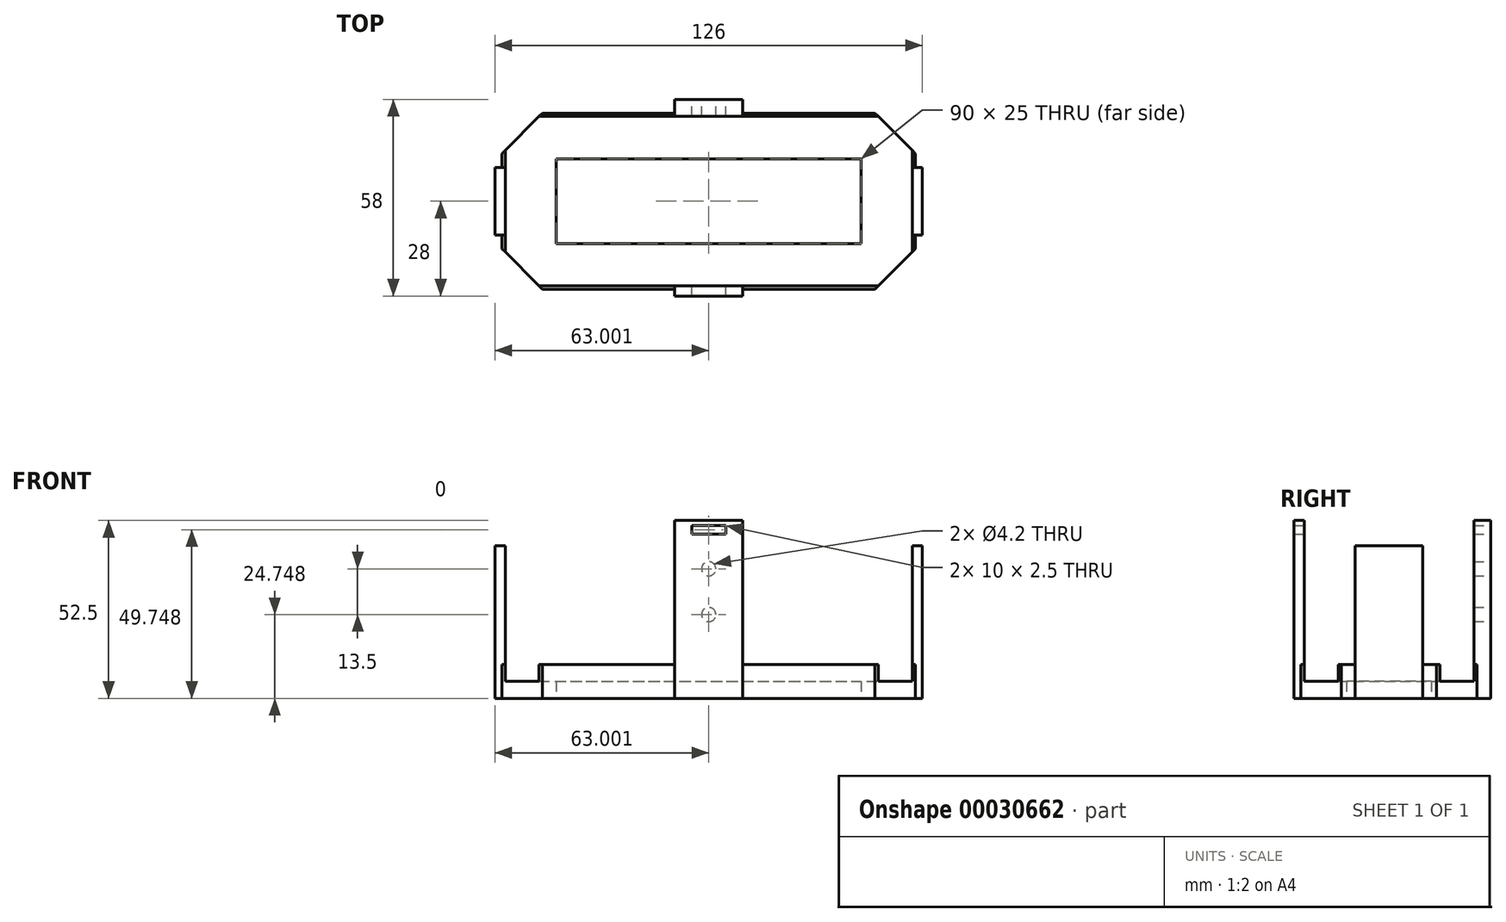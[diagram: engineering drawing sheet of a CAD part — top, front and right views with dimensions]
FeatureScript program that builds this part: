
annotation { "Feature Type Name" : "Feature", "Feature Type Description" : "" }
export const myFeature = defineFeature(function(context is Context, id is Id, definition is map)
    precondition{}
    {
        {
            var Q0;
            Q0=qCreatedBy(makeId("Front.planeOp"),FACE);
            var sketch = newSketch(context, id + "F0", { "sketchPlane" : qUnion([Q0])});
            skLineSegment(sketch, "E0.0.0", {"start": v(107.73, 27.2) * mm, "end": v(107.73, -17.8) * mm});
            skLineSegment(sketch, "E0.0.1", {"start": v(107.73, -17.8) * mm, "end": v(127.73, -17.8) * mm});
            skLineSegment(sketch, "E0.0.2", {"start": v(127.73, -17.8) * mm, "end": v(127.73, 27.2) * mm});
            skLineSegment(sketch, "E0.0.3", {"start": v(127.73, 27.2) * mm, "end": v(107.73, 27.2) * mm});
            skPoint(sketch, "E1", {"position": v(117.73, -17.8) * mm});
            skPoint(sketch, "E2", {"position": v(117.73, 27.2) * mm});
            skLineSegment(sketch, "E3.0.2", {"start": v(24.49, -17.8) * mm, "end": v(24.49, 9.2) * mm});
            skCircle(sketch, "E4.MirrorC", {"center": v(117.73, 20.46) * mm, "radius": 2.1 * mm});
            skCircle(sketch, "E5.MirrorC", {"center": v(117.73, 6.96) * mm, "radius": 2.1 * mm});
            skLineSegment(sketch, "E6.bottom", {"start": v(57.73, -12.8) * mm, "end": v(177.73, -12.8) * mm});
            skLineSegment(sketch, "E6.top", {"start": v(57.73, -17.8) * mm, "end": v(177.73, -17.8) * mm});
            skLineSegment(sketch, "E6.left", {"start": v(57.73, -12.8) * mm, "end": v(57.73, -17.8) * mm});
            skLineSegment(sketch, "E6.right", {"start": v(177.73, -12.8) * mm, "end": v(177.73, -17.8) * mm});
            skLineSegment(sketch, "E7", {"start": v(107.73, -17.8) * mm, "end": v(57.73, -12.8) * mm, "construction": true});
            skLineSegment(sketch, "E8", {"start": v(127.73, -17.8) * mm, "end": v(177.73, -12.8) * mm, "construction": true});
            skSolve(sketch);
        }
        {
            var Q0;
            {var subQ0=sQuery(id+"F0.wireOp",EDGE,"E0.0.3");Q0=makeQuery(id+"F0.imprint","IMPRINT",FACE,{"disambiguationData":[TD([[makeQuery(id+"F0.imprint","IMPRINT",EDGE,{"derivedFrom":subQ0}),1.0]])]});}
            var Q1;
            {var subQ0=sQuery(id+"F0.wireOp",EDGE,"E6.top");var subQ1=sQuery(id+"F0.wireOp",EDGE,"E0.0.0");var subQ2=makeQuery(id+"F0.imprint","INTERSECT",VERTEX,{"derivedFrom":[subQ1,subQ0]});Q1=makeQuery(id+"F0.imprint","IMPRINT",FACE,{"disambiguationData":[TD([[makeQuery(id+"F0.imprint","IMPRINT",EDGE,{"disambiguationData":[TD([[subQ2,1.0]])],"derivedFrom":subQ1}),1.0]])]});}
            extrude(context, id + "F1", {"entities" : qUnion([Q0, Q1]), "depth" : 5 * mm});
        }
        {
            var Q0;
            {var subQ5=sQuery(id+"F0.wireOp",EDGE,"E6.left");Q0=makeQuery(id+"F0.imprint","IMPRINT",FACE,{"disambiguationData":[TD([[makeQuery(id+"F0.imprint","IMPRINT",EDGE,{"derivedFrom":subQ5}),1.0]])]});}
            var Q1;
            {var subQ5=sQuery(id+"F0.wireOp",EDGE,"E6.right");Q1=makeQuery(id+"F0.imprint","IMPRINT",FACE,{"disambiguationData":[TD([[makeQuery(id+"F0.imprint","IMPRINT",EDGE,{"derivedFrom":subQ5}),-1.0]])]});}
            var Q2;
            {var subQ0=sQuery(id+"F0.wireOp",EDGE,"E6.top");var subQ1=sQuery(id+"F0.wireOp",EDGE,"E0.0.0");var subQ2=makeQuery(id+"F0.imprint","INTERSECT",VERTEX,{"derivedFrom":[subQ1,subQ0]});Q2=makeQuery(id+"F0.imprint","IMPRINT",FACE,{"disambiguationData":[TD([[makeQuery(id+"F0.imprint","IMPRINT",EDGE,{"disambiguationData":[TD([[subQ2,1.0]])],"derivedFrom":subQ1}),1.0]])]});}
            var Q3;
            Q3=makeQuery(id+"F1.opExtrude","CAP_FACE",FACE,{"disambiguationData":[OSD([sQuery(id+"F0.wireOp",EDGE,"E0.0.0"),sQuery(id+"F0.wireOp",EDGE,"E0.0.2"),sQuery(id+"F0.wireOp",EDGE,"E0.0.3"),sQuery(id+"F0.wireOp",EDGE,"E4.MirrorC"),sQuery(id+"F0.wireOp",EDGE,"E5.MirrorC"),sQuery(id+"F0.wireOp",EDGE,"E6.top")])],"isStart":false});
            extrude(context, id + "F2", {"entities" : qUnion([Q0, Q1, Q2]), "operationType" : NewBodyOperationType.ADD, "depth" : 55 * mm, "hasSecondDirection" : true, "secondDirectionBound" : BoundingType.UP_TO_SURFACE, "secondDirectionOppositeDirection" : false, "secondDirectionBoundEntityFace" : qUnion([Q3]), "secondDirectionDepth" : 25 * mm});
        }
        {
            var Q0;
            {var subQ0=sQuery(id+"F0.wireOp",EDGE,"E0.0.3");Q0=makeQuery(id+"F0.imprint","IMPRINT",FACE,{"disambiguationData":[TD([[makeQuery(id+"F0.imprint","IMPRINT",EDGE,{"derivedFrom":subQ0}),1.0]])]});}
            var Q1;
            {var subQ0=sQuery(id+"F0.wireOp",EDGE,"E6.top");var subQ1=sQuery(id+"F0.wireOp",EDGE,"E0.0.0");var subQ2=makeQuery(id+"F0.imprint","INTERSECT",VERTEX,{"derivedFrom":[subQ1,subQ0]});Q1=makeQuery(id+"F0.imprint","IMPRINT",FACE,{"disambiguationData":[TD([[makeQuery(id+"F0.imprint","IMPRINT",EDGE,{"disambiguationData":[TD([[subQ2,1.0]])],"derivedFrom":subQ1}),1.0]])]});}
            var Q2;
            Q2=makeQuery(id+"F0.imprint","IMPRINT",FACE,{"disambiguationData":[TD([[makeQuery(id+"F0.imprint","IMPRINT",EDGE,{"derivedFrom":sQuery(id+"F0.wireOp",EDGE,"E4.MirrorC")}),1.0]])]});
            var Q3;
            Q3=makeQuery(id+"F0.imprint","IMPRINT",FACE,{"disambiguationData":[TD([[makeQuery(id+"F0.imprint","IMPRINT",EDGE,{"derivedFrom":sQuery(id+"F0.wireOp",EDGE,"E5.MirrorC")}),1.0]])]});
            var Q4;
            Q4=makeQuery(id+"F2.opExtrude","CAP_FACE",FACE,{"disambiguationData":[OSD([sQuery(id+"F0.wireOp",EDGE,"E6.bottom"),sQuery(id+"F0.wireOp",EDGE,"E6.top"),sQuery(id+"F0.wireOp",EDGE,"E6.left"),sQuery(id+"F0.wireOp",EDGE,"E6.right")])],"isStart":false});
            extrude(context, id + "F3", {"entities" : qUnion([Q0, Q1, Q2, Q3]), "operationType" : NewBodyOperationType.ADD, "depth" : 58 * mm, "hasSecondDirection" : true, "secondDirectionBound" : BoundingType.UP_TO_SURFACE, "secondDirectionOppositeDirection" : false, "secondDirectionBoundEntityFace" : qUnion([Q4]), "secondDirectionDepth" : 25 * mm});
        }
        {
            var Q0;
            Q0=makeQuery(id+"F2.opExtrude","SWEPT_FACE",FACE,{"disambiguationData":[OSD([sQuery(id+"F0.wireOp",EDGE,"E6.left")])]});
            var sketch = newSketch(context, id + "F4", { "sketchPlane" : qUnion([Q0])});
            skLineSegment(sketch, "E9.bottom", {"start": v(20, 27.2) * mm, "end": v(40, 27.2) * mm});
            skLineSegment(sketch, "E9.top", {"start": v(20, -17.8) * mm, "end": v(40, -17.8) * mm});
            skLineSegment(sketch, "E9.left", {"start": v(20, 27.2) * mm, "end": v(20, -17.8) * mm});
            skLineSegment(sketch, "E9.right", {"start": v(40, 27.2) * mm, "end": v(40, -17.8) * mm});
            skLineSegment(sketch, "E10", {"start": v(20, -17.8) * mm, "end": v(5, -17.8) * mm, "construction": true});
            skLineSegment(sketch, "E11", {"start": v(40, -17.8) * mm, "end": v(55, -17.8) * mm, "construction": true});
            skSolve(sketch);
        }
        {
            var Q0;
            {var subQ0=sQuery(id+"F4.wireOp",EDGE,"E9.bottom");Q0=makeQuery(id+"F4.imprint","IMPRINT",FACE,{"disambiguationData":[TD([[makeQuery(id+"F4.imprint","IMPRINT",EDGE,{"derivedFrom":subQ0}),-1.0]])]});}
            var Q1;
            {var subQ0=sQuery(id+"F4.wireOp",EDGE,"E9.top");Q1=makeQuery(id+"F4.imprint","IMPRINT",FACE,{"disambiguationData":[TD([[makeQuery(id+"F4.imprint","IMPRINT",EDGE,{"derivedFrom":subQ0}),-1.0]])]});}
            extrude(context, id + "F5", {"entities" : qUnion([Q0, Q1]), "operationType" : NewBodyOperationType.ADD, "depth" : 3 * mm});
        }
        {
            var Q0;
            Q0=makeQuery(id+"F5.opExtrude","CAP_FACE",FACE,{"disambiguationData":[OSD([sQuery(id+"F4.wireOp",EDGE,"E9.bottom"),sQuery(id+"F4.wireOp",EDGE,"E9.top"),sQuery(id+"F4.wireOp",EDGE,"E9.left"),sQuery(id+"F4.wireOp",EDGE,"E9.right")])],"isStart":false});
            var Q1;
            Q1=makeQuery(id+"F2.opExtrude","SWEPT_FACE",FACE,{"disambiguationData":[OSD([sQuery(id+"F0.wireOp",EDGE,"E6.right")])]});
            extrude(context, id + "F6", {"entities" : qUnion([Q0]), "operationType" : NewBodyOperationType.ADD, "oppositeDirection" : true, "depth" : 126 * mm, "hasSecondDirection" : true, "secondDirectionBound" : BoundingType.UP_TO_SURFACE, "secondDirectionOppositeDirection" : true, "secondDirectionBoundEntityFace" : qUnion([Q1]), "secondDirectionDepth" : 276 * mm});
        }
        {
            var Q0;
            Q0=makeQuery(id+"F2.opExtrude","SWEPT_FACE",FACE,{"disambiguationData":[OSD([sQuery(id+"F0.wireOp",EDGE,"E6.bottom")])]});
            var sketch = newSketch(context, id + "F7", { "sketchPlane" : qUnion([Q0])});
            skLineSegment(sketch, "E12.bottom", {"start": v(56.73, -4) * mm, "end": v(178.73, -4) * mm});
            skLineSegment(sketch, "E12.top", {"start": v(56.73, -56) * mm, "end": v(178.73, -56) * mm});
            skLineSegment(sketch, "E12.left", {"start": v(56.73, -4) * mm, "end": v(56.73, -56) * mm});
            skLineSegment(sketch, "E12.right", {"start": v(178.73, -4) * mm, "end": v(178.73, -56) * mm});
            skSolve(sketch);
        }
        {
            var Q0;
            Q0=makeQuery(id+"F7.imprint","IMPRINT",FACE,{"disambiguationData":[TD([[makeQuery(id+"F7.imprint","IMPRINT",EDGE,{"derivedFrom":sQuery(id+"F7.wireOp",EDGE,"E12.bottom")}),-1.0]])]});
            extrude(context, id + "F8", {"entities" : qUnion([Q0]), "operationType" : NewBodyOperationType.ADD, "depth" : 5 * mm, "hasSecondDirection" : true, "secondDirectionOppositeDirection" : true, "secondDirectionDepth" : 5 * mm});
        }
        {
            var Q0;
            Q0=makeQuery(id+"F1.opExtrude","SWEPT_FACE",FACE,{"disambiguationData":[OSD([sQuery(id+"F0.wireOp",EDGE,"E0.0.3")])]});
            var Q1;
            Q1=makeQuery(id+"F3.opExtrude","SWEPT_FACE",FACE,{"disambiguationData":[OSD([sQuery(id+"F0.wireOp",EDGE,"E0.0.3")])]});
            extrude(context, id + "F9", {"entities" : qUnion([Q0, Q1]), "operationType" : NewBodyOperationType.ADD, "depth" : 7.5 * mm});
        }
        {
            var Q0;
            {var subQ0=sQuery(id+"F0.wireOp",EDGE,"E0.0.3");Q0=makeQuery(id+"F9.boolean.opBoolean","MERGE",FACE,{"derivedFrom":[makeQuery(id+"F1.opExtrude","CAP_FACE",FACE,{"disambiguationData":[OSD([sQuery(id+"F0.wireOp",EDGE,"E0.0.0"),sQuery(id+"F0.wireOp",EDGE,"E0.0.2"),subQ0,sQuery(id+"F0.wireOp",EDGE,"E4.MirrorC"),sQuery(id+"F0.wireOp",EDGE,"E5.MirrorC"),sQuery(id+"F0.wireOp",EDGE,"E6.top")])],"isStart":true}),makeQuery(id+"F9.opExtrude","SWEPT_FACE",FACE,{"disambiguationData":[OSD([subQ0]),TDD([makeQuery(id+"F1.opExtrude","CAP_EDGE",EDGE,{"disambiguationData":[OSD([subQ0])],"isStart":true})])]})]});}
            var sketch = newSketch(context, id + "F10", { "sketchPlane" : qUnion([Q0])});
            skLineSegment(sketch, "E13.bottom", {"start": v(-122.73, 33.2) * mm, "end": v(-112.73, 33.2) * mm});
            skLineSegment(sketch, "E13.top", {"start": v(-122.73, 30.7) * mm, "end": v(-112.73, 30.7) * mm});
            skLineSegment(sketch, "E13.left", {"start": v(-122.73, 33.2) * mm, "end": v(-122.73, 30.7) * mm});
            skLineSegment(sketch, "E13.right", {"start": v(-112.73, 33.2) * mm, "end": v(-112.73, 30.7) * mm});
            skLineSegment(sketch, "E14.0", {"start": v(-127.73, 27.2) * mm, "end": v(-107.73, 27.2) * mm, "construction": true});
            skLineSegment(sketch, "E15", {"start": v(-122.73, 31.96) * mm, "end": v(-127.73, 31.96) * mm, "construction": true});
            skLineSegment(sketch, "E16", {"start": v(-112.73, 31.96) * mm, "end": v(-107.73, 31.96) * mm, "construction": true});
            skSolve(sketch);
        }
        {
            var Q0;
            Q0=makeQuery(id+"F10.imprint","IMPRINT",FACE,{"disambiguationData":[TD([[makeQuery(id+"F10.imprint","IMPRINT",EDGE,{"derivedFrom":sQuery(id+"F10.wireOp",EDGE,"E13.bottom")}),-1.0]])]});
            var Q1;
            {var subQ0=sQuery(id+"F0.wireOp",EDGE,"E0.0.3");Q1=makeQuery(id+"F9.boolean.opBoolean","MERGE",FACE,{"derivedFrom":[makeQuery(id+"F3.opExtrude","CAP_FACE",FACE,{"disambiguationData":[OSD([sQuery(id+"F0.wireOp",EDGE,"E0.0.0"),sQuery(id+"F0.wireOp",EDGE,"E0.0.2"),subQ0,sQuery(id+"F0.wireOp",EDGE,"E6.top")])],"isStart":false}),makeQuery(id+"F9.opExtrude","SWEPT_FACE",FACE,{"disambiguationData":[OSD([subQ0]),TDD([makeQuery(id+"F3.opExtrude","CAP_EDGE",EDGE,{"disambiguationData":[OSD([subQ0])],"isStart":false})])]})]});}
            extrude(context, id + "F11", {"entities" : qUnion([Q0]), "operationType" : NewBodyOperationType.REMOVE, "endBound" : BoundingType.UP_TO_SURFACE, "oppositeDirection" : true, "endBoundEntityFace" : qUnion([Q1]), "depth" : 25 * mm});
        }
        {
            var Q0;
            {var subQ0=sQuery(id+"F4.wireOp",EDGE,"E9.top");var subQ1=sQuery(id+"F0.wireOp",EDGE,"E6.top");Q0=makeQuery(id+"F8.boolean.opBoolean","MERGE",FACE,{"derivedFrom":[makeQuery(id+"F6.boolean.opBoolean","MERGE",FACE,{"derivedFrom":[makeQuery(id+"F5.boolean.opBoolean","MERGE",FACE,{"derivedFrom":[makeQuery(id+"F3.boolean.opBoolean","MERGE",FACE,{"derivedFrom":[makeQuery(id+"F2.boolean.opBoolean","MERGE",FACE,{"derivedFrom":[makeQuery(id+"F1.opExtrude","SWEPT_FACE",FACE,{"disambiguationData":[OSD([subQ1])]}),makeQuery(id+"F2.opExtrude","SWEPT_FACE",FACE,{"disambiguationData":[OSD([subQ1])]})]}),makeQuery(id+"F3.opExtrude","SWEPT_FACE",FACE,{"disambiguationData":[OSD([subQ1])]})]}),makeQuery(id+"F5.opExtrude","SWEPT_FACE",FACE,{"disambiguationData":[OSD([subQ0])]})]}),makeQuery(id+"F6.opExtrude","SWEPT_FACE",FACE,{"disambiguationData":[OSD([subQ0])]})]}),makeQuery(id+"F8.opExtrude","CAP_FACE",FACE,{"disambiguationData":[OSD([sQuery(id+"F0.wireOp",EDGE,"E6.bottom"),sQuery(id+"F0.wireOp",EDGE,"E6.left"),sQuery(id+"F0.wireOp",EDGE,"E6.right"),sQuery(id+"F7.wireOp",EDGE,"E12.bottom"),sQuery(id+"F7.wireOp",EDGE,"E12.top"),sQuery(id+"F7.wireOp",EDGE,"E12.left"),sQuery(id+"F7.wireOp",EDGE,"E12.right")])],"isStart":true})]});}
            var sketch = newSketch(context, id + "F12", { "sketchPlane" : qUnion([Q0])});
            skLineSegment(sketch, "E17.0.0", {"start": v(127.73, 0) * mm, "end": v(127.73, 4) * mm});
            skLineSegment(sketch, "E17.0.1", {"start": v(127.73, 4) * mm, "end": v(178.73, 4) * mm});
            skLineSegment(sketch, "E17.0.2", {"start": v(178.73, 4) * mm, "end": v(178.73, 20) * mm});
            skLineSegment(sketch, "E17.0.3", {"start": v(178.73, 20) * mm, "end": v(180.73, 20) * mm});
            skLineSegment(sketch, "E17.0.4", {"start": v(180.73, 20) * mm, "end": v(180.73, 40) * mm});
            skLineSegment(sketch, "E17.0.5", {"start": v(180.73, 40) * mm, "end": v(178.73, 40) * mm});
            skLineSegment(sketch, "E17.0.6", {"start": v(178.73, 40) * mm, "end": v(178.73, 56) * mm});
            skLineSegment(sketch, "E17.0.7", {"start": v(178.73, 56) * mm, "end": v(127.73, 56) * mm});
            skLineSegment(sketch, "E17.0.8", {"start": v(127.73, 56) * mm, "end": v(127.73, 58) * mm});
            skLineSegment(sketch, "E17.0.9", {"start": v(127.73, 58) * mm, "end": v(107.73, 58) * mm});
            skLineSegment(sketch, "E17.0.10", {"start": v(107.73, 58) * mm, "end": v(107.73, 56) * mm});
            skLineSegment(sketch, "E17.0.11", {"start": v(107.73, 56) * mm, "end": v(56.73, 56) * mm});
            skLineSegment(sketch, "E17.0.12", {"start": v(56.73, 56) * mm, "end": v(56.73, 40) * mm});
            skLineSegment(sketch, "E17.0.13", {"start": v(56.73, 40) * mm, "end": v(54.73, 40) * mm});
            skLineSegment(sketch, "E17.0.14", {"start": v(54.73, 40) * mm, "end": v(54.73, 20) * mm});
            skLineSegment(sketch, "E17.0.15", {"start": v(54.73, 20) * mm, "end": v(56.73, 20) * mm});
            skLineSegment(sketch, "E17.0.16", {"start": v(56.73, 20) * mm, "end": v(56.73, 4) * mm});
            skLineSegment(sketch, "E17.0.17", {"start": v(56.73, 4) * mm, "end": v(107.73, 4) * mm});
            skLineSegment(sketch, "E17.0.18", {"start": v(107.73, 4) * mm, "end": v(107.73, 0) * mm});
            skLineSegment(sketch, "E17.0.19", {"start": v(107.73, 0) * mm, "end": v(127.73, 0) * mm});
            skPoint(sketch, "E18", {"position": v(56.73, 16) * mm});
            skLineSegment(sketch, "E19", {"start": v(56.73, 16) * mm, "end": v(68.73, 4) * mm});
            skLineSegment(sketch, "E20", {"start": v(54.73, 30) * mm, "end": v(180.73, 30) * mm, "construction": true});
            skLineSegment(sketch, "E21", {"start": v(117.73, 0) * mm, "end": v(117.73, 58) * mm, "construction": true});
            skLineSegment(sketch, "E22.MirrorCS", {"start": v(56.73, 44) * mm, "end": v(68.73, 56) * mm});
            skLineSegment(sketch, "E23.MirrorCS", {"start": v(178.73, 44) * mm, "end": v(166.73, 56) * mm});
            skLineSegment(sketch, "E24.MirrorCS", {"start": v(178.73, 16) * mm, "end": v(166.73, 4) * mm});
            skLineSegment(sketch, "E25.bottom", {"start": v(162.73, 42.5) * mm, "end": v(72.73, 42.5) * mm});
            skLineSegment(sketch, "E25.top", {"start": v(162.73, 17.5) * mm, "end": v(72.73, 17.5) * mm});
            skLineSegment(sketch, "E25.left", {"start": v(162.73, 42.5) * mm, "end": v(162.73, 17.5) * mm});
            skLineSegment(sketch, "E25.right", {"start": v(72.73, 42.5) * mm, "end": v(72.73, 17.5) * mm});
            skPoint(sketch, "E25.middle", {"position": v(117.73, 30) * mm});
            skSolve(sketch);
        }
        {
            var Q0;
            {var subQ3=sQuery(id+"F12.wireOp",EDGE,"E19");Q0=makeQuery(id+"F12.imprint","IMPRINT",FACE,{"disambiguationData":[TD([[makeQuery(id+"F12.imprint","IMPRINT",EDGE,{"derivedFrom":subQ3}),-1.0]])]});}
            var Q1;
            {var subQ3=sQuery(id+"F12.wireOp",EDGE,"E22.MirrorCS");Q1=makeQuery(id+"F12.imprint","IMPRINT",FACE,{"disambiguationData":[TD([[makeQuery(id+"F12.imprint","IMPRINT",EDGE,{"derivedFrom":subQ3}),1.0]])]});}
            var Q2;
            {var subQ3=sQuery(id+"F12.wireOp",EDGE,"E23.MirrorCS");Q2=makeQuery(id+"F12.imprint","IMPRINT",FACE,{"disambiguationData":[TD([[makeQuery(id+"F12.imprint","IMPRINT",EDGE,{"derivedFrom":subQ3}),-1.0]])]});}
            var Q3;
            {var subQ3=sQuery(id+"F12.wireOp",EDGE,"E24.MirrorCS");Q3=makeQuery(id+"F12.imprint","IMPRINT",FACE,{"disambiguationData":[TD([[makeQuery(id+"F12.imprint","IMPRINT",EDGE,{"derivedFrom":subQ3}),1.0]])]});}
            var Q4;
            Q4=makeQuery(id+"F12.imprint","IMPRINT",FACE,{"disambiguationData":[TD([[makeQuery(id+"F12.imprint","IMPRINT",EDGE,{"derivedFrom":sQuery(id+"F12.wireOp",EDGE,"E25.bottom")}),1.0]])]});
            var Q5;
            {var subQ3=sQuery(id+"F0.wireOp",EDGE,"E0.0.0");var subQ5=makeQuery(id+"F3.opExtrude","SWEPT_FACE",FACE,{"disambiguationData":[OSD([subQ3])]});var subQ6=sQuery(id+"F7.wireOp",EDGE,"E12.top");var subQ7=sQuery(id+"F7.wireOp",EDGE,"E12.left");var subQ8=sQuery(id+"F0.wireOp",EDGE,"E6.right");var subQ9=sQuery(id+"F0.wireOp",EDGE,"E6.left");var subQ10=sQuery(id+"F0.wireOp",EDGE,"E6.bottom");Q5=makeQuery(id+"F8.boolean.opBoolean","SPLIT",FACE,{"disambiguationData":[TD([subQ5])],"derivedFrom":makeQuery(id+"F8.opExtrude","CAP_FACE",FACE,{"disambiguationData":[OSD([subQ10,subQ9,subQ8,sQuery(id+"F7.wireOp",EDGE,"E12.bottom"),subQ6,subQ7,sQuery(id+"F7.wireOp",EDGE,"E12.right")])],"isStart":false})});}
            extrude(context, id + "F13", {"entities" : qUnion([Q0, Q1, Q2, Q3, Q4]), "operationType" : NewBodyOperationType.REMOVE, "endBound" : BoundingType.UP_TO_SURFACE, "oppositeDirection" : true, "endBoundEntityFace" : qUnion([Q5]), "depth" : 25 * mm});
        }
    });
